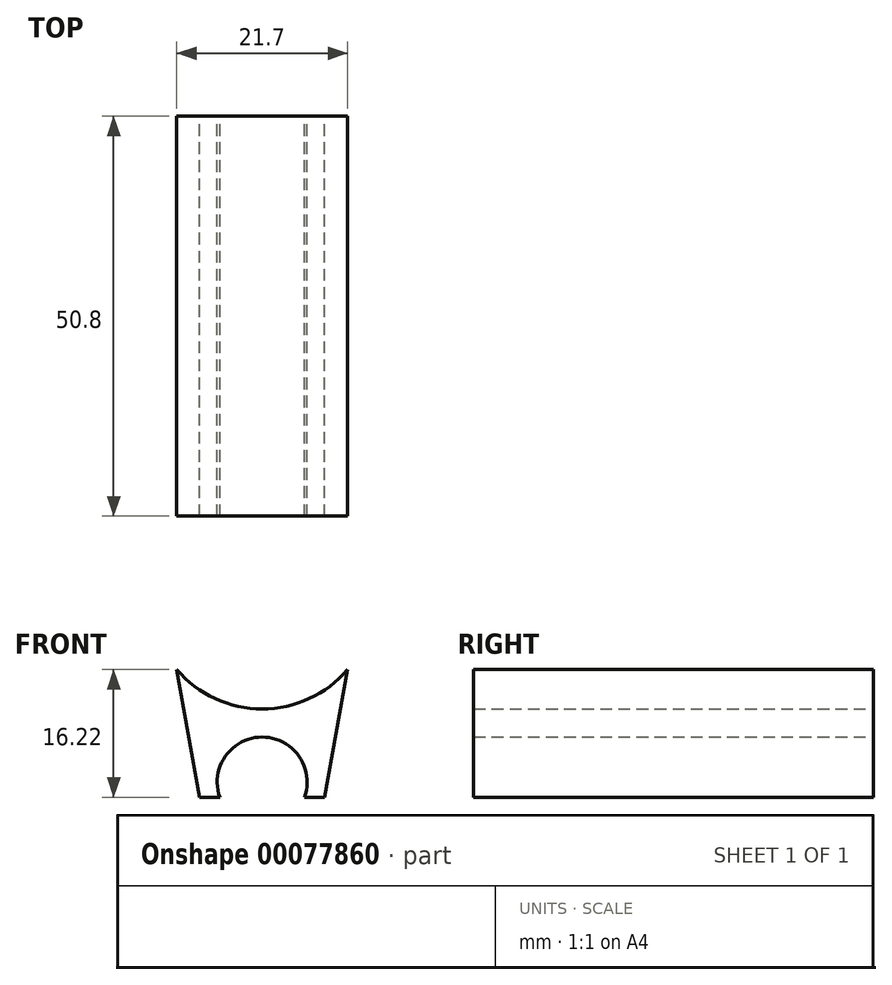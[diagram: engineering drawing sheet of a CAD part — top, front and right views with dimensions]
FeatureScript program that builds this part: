
annotation { "Feature Type Name" : "Feature", "Feature Type Description" : "" }
export const myFeature = defineFeature(function(context is Context, id is Id, definition is map)
    precondition{}
    {
        {
            var Q0;
            Q0=qCreatedBy(makeId("Front.planeOp"),FACE);
            var sketch = newSketch(context, id + "F0", { "sketchPlane" : qUnion([Q0])});
            skLineSegment(sketch, "E0", {"start": v(10.85, 14.29) * mm, "end": v(7.94, -1.93) * mm});
            skLineSegment(sketch, "E1", {"start": v(7.94, -1.93) * mm, "end": v(-7.94, -1.93) * mm});
            skLineSegment(sketch, "E2", {"start": v(-7.94, -1.93) * mm, "end": v(-10.85, 14.29) * mm});
            skCircle(sketch, "E3", {"center": v(0, 0) * mm, "radius": 5.72 * mm});
            skArc(sketch, "E4", {"start": v(-10.85, 14.29) * mm, "mid": v(0, 9.3) * mm, "end": v(10.85, 14.29) * mm});
            skLineSegment(sketch, "E5", {"start": v(-10.85, 14.29) * mm, "end": v(10.85, 14.29) * mm});
            skSolve(sketch);
        }
        {
            var Q0;
            Q0=makeQuery(id+"F0.imprint","IMPRINT",FACE,{"disambiguationData":[TD([[makeQuery(id+"F0.imprint","IMPRINT",EDGE,{"derivedFrom":sQuery(id+"F0.wireOp",EDGE,"R4Fj1xyU-wPE3-fLBo-3pYN-34EC6WKIEC9R")}),-1.0]])]});
            var Q1;
            {var subQ4=sQuery(id+"F0.wireOp",EDGE,"E0");Q1=makeQuery(id+"F0.imprint","IMPRINT",FACE,{"disambiguationData":[TD([[makeQuery(id+"F0.imprint","IMPRINT",EDGE,{"derivedFrom":subQ4}),-1.0]])]});}
            extrude(context, id + "F1", {"entities" : qUnion([Q0, Q1]), "depth" : 50.8 * mm});
        }
    });
